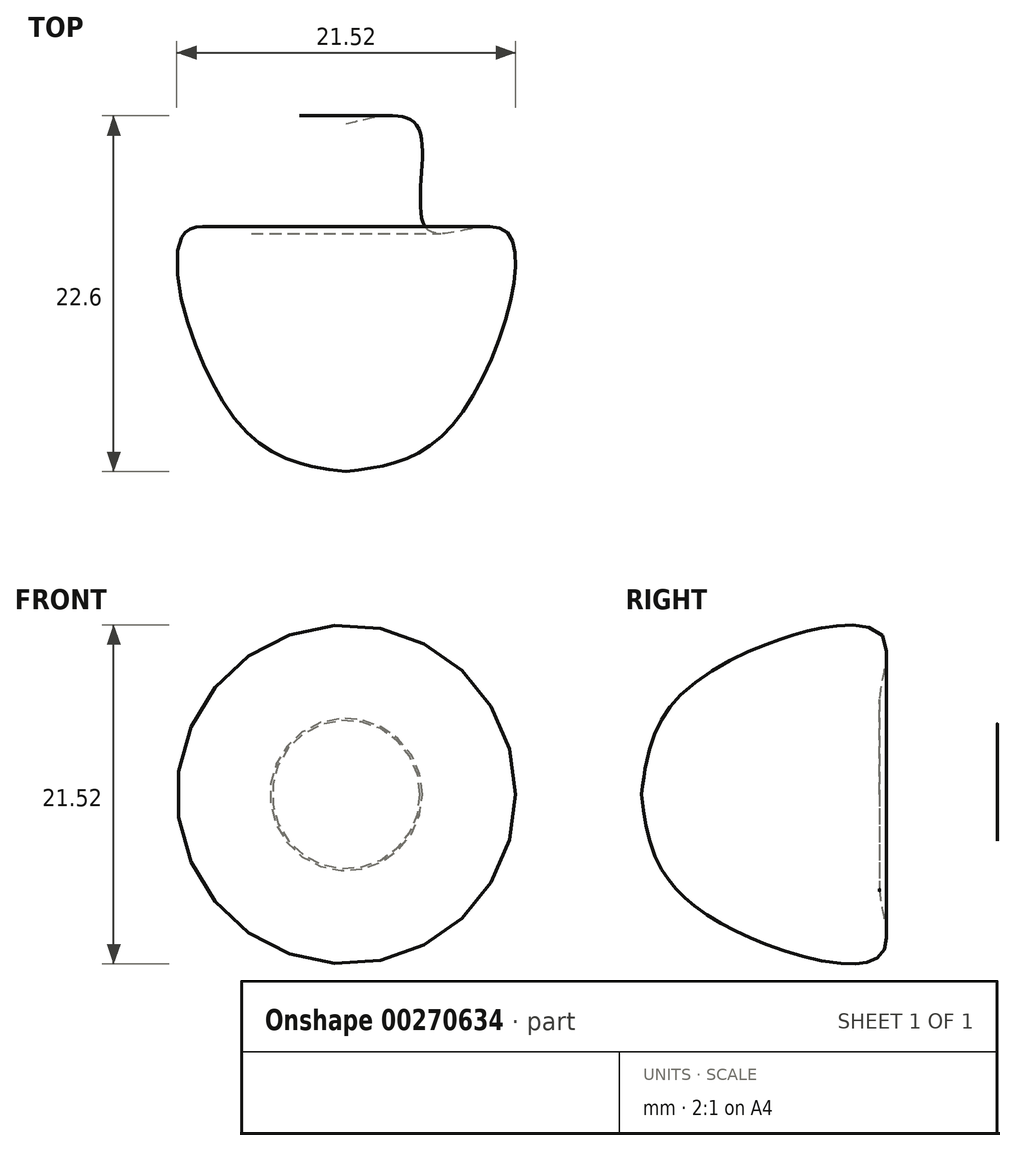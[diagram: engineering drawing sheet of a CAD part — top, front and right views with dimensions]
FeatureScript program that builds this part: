
annotation { "Feature Type Name" : "Feature", "Feature Type Description" : "" }
export const myFeature = defineFeature(function(context is Context, id is Id, definition is map)
    precondition{}
    {
        {
            var Q0;
            Q0=qCreatedBy(makeId("Top.planeOp"),FACE);
            var sketch = newSketch(context, id + "F0", { "sketchPlane" : qUnion([Q0])});
            skLineSegment(sketch, "E0", {"start": v(0, 4.6) * mm, "end": v(0, -3.32) * mm});
            skFitSpline(sketch, "E1", {"points": [v(0, -3.32) * mm, v(7.05, 0) * mm, v(10.07, 12) * mm, v(5.2, 12.03) * mm, v(4.6, 18.46) * mm, v(0, 18.75) * mm], "startDerivative": vector(34.9, 4.22) * mm, "endDerivative": vector(-36.88, -9.11) * mm});
            skLineSegment(sketch, "E2", {"start": v(0, 4.6) * mm, "end": v(0, 18.75) * mm});
            skSolve(sketch);
        }
        {
            var Q0;
            Q0=makeQuery(id+"F0.imprint","IMPRINT",FACE,{"disambiguationData":[TD([[makeQuery(id+"F0.imprint","IMPRINT",EDGE,{"derivedFrom":sQuery(id+"F0.wireOp",EDGE,"E0")}),1.0]])]});
            var Q1;
            Q1=sQuery(id+"F0.wireOp",EDGE,"E0");
            revolve(context, id + "F1", {"entities" : qUnion([Q0]), "axis" : qUnion([Q1]), "revolveType" : RevolveType.FULL});
        }
    });
